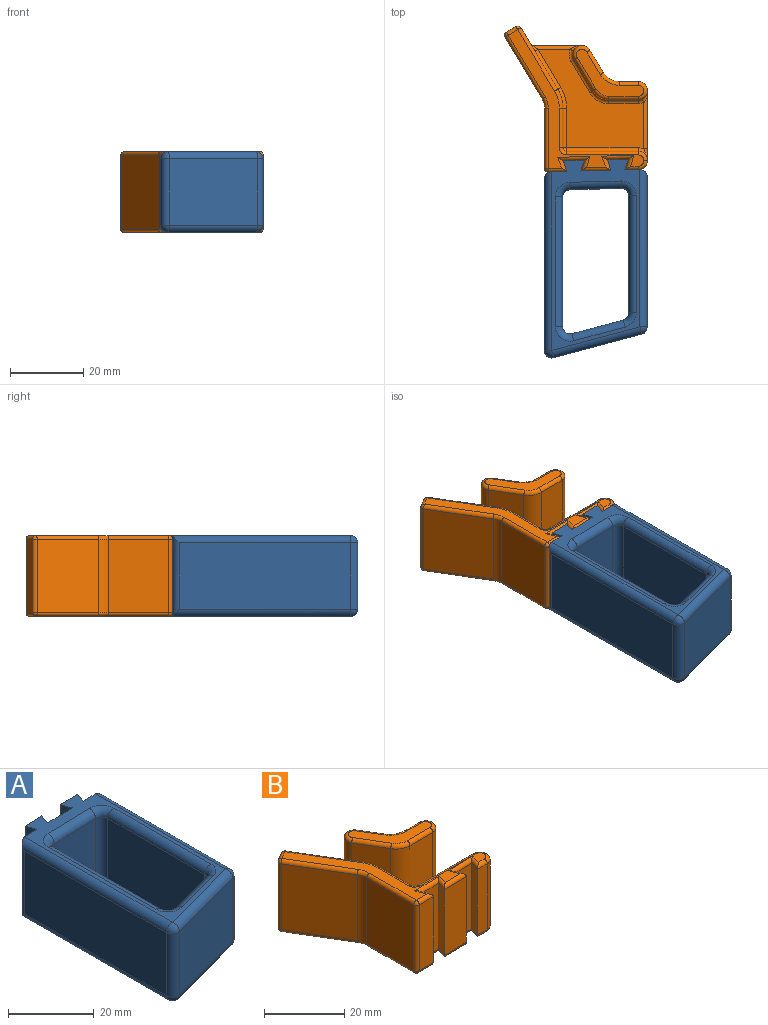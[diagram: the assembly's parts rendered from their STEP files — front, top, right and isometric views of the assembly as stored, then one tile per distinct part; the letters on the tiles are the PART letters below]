
ASSEMBLY  parts=2 mates=1
PART A: 52 faces, bbox 28x54.2x22 mm
  f0: plane 52.16x24.01mm, normal (0,0,-1), area 222.9mm2, adj f5,f6,f7,f8,f9,f13,f14,f15
  f1: plane 52.16x24.01mm, normal (0,0,1), area 222.9mm2, adj f5,f6,f7,f8,f9,f13,f14,f15
  f2: plane 35.33x18mm, normal (1,0,0), area 635.9mm2, adj f18,f21,f25,f26
  f3: plane 18x14.01mm, normal (0.03,-1,0), area 252.2mm2, adj f24,f25,f33,f34
  f4: plane 31.94x18mm, normal (-1,0,0), area 574.9mm2, adj f23,f32,f33,f37
  f5: plane 22x8.21mm, normal (-0.03,1,0), area 180.7mm2, adj f0,f1,f6,f16
  f6: plane 22x2.93mm, normal (0.95,-0.31,0), area 67.8mm2, adj f0,f1,f5,f7
  f7: plane 22x5.72mm, normal (-0.03,1,0), area 125.9mm2, adj f0,f1,f6,f8
  f8: plane 22x2.88mm, normal (-0.95,-0.32,0), area 66.7mm2, adj f0,f1,f7,f9
  f9: plane 22x4.2mm, normal (-0.03,1,0), area 92.4mm2, adj f0,f1,f8,f49,f50,f51
  f10: plane 46.71x18mm, normal (-1,0,0), area 840.9mm2, adj f45,f49,f50,f51
  f11: plane 24.01x18mm, normal (0.26,-0.97,0), area 447.3mm2, adj f40,f44,f45,f46
  f12: plane 40.91x18mm, normal (1,0,0), area 736.4mm2, adj f38,f39,f40,f41
  f13: plane 22x4.02mm, normal (-0.03,1,0), area 88.4mm2, adj f0,f1,f14,f38
  f14: plane 22x2.93mm, normal (0.95,-0.31,0), area 67.8mm2, adj f0,f1,f13,f15
  f15: plane 22x5.72mm, normal (-0.03,1,0), area 126mm2, adj f0,f1,f14,f16
  f16: plane 22x2.88mm, normal (-0.95,-0.32,0), area 66.8mm2, adj f0,f1,f5,f15
  f17: plane 18x14.01mm, normal (-0.26,0.97,0), area 261mm2, adj f21,f22,f31,f32
  f18: cylinder r=2mm len=35.33mm, axis (0,1,0), area 111mm2, adj f0,f2,f19,f20
  f19: torus R=4mm, axis (0,0,1), area 15.7mm2, adj f0,f18,f21,f22
  f20: torus R=4mm, axis (0,0,1), area 13.2mm2, adj f0,f18,f24,f25
  f21: cylinder r=2mm len=18mm, axis (0,0,1), area 66mm2, adj f2,f17,f19,f27
  f22: cylinder r=2mm len=14.52mm, axis (-0.97,-0.26,0), area 45.6mm2, adj f0,f17,f19,f28
  f23: cylinder r=2mm len=31.94mm, axis (0,-1,0), area 100.3mm2, adj f0,f4,f28,f29
  f24: cylinder r=2mm len=14.06mm, axis (1,0.03,0), area 44mm2, adj f0,f3,f20,f29
  f25: cylinder r=2mm len=18mm, axis (0,0,1), area 55.6mm2, adj f2,f3,f20,f30
  f26: cylinder r=2mm len=35.33mm, axis (0,-1,0), area 111mm2, adj f1,f2,f27,f30
  f27: torus R=4mm, axis (0,0,1), area 15.7mm2, adj f1,f21,f26,f31
  f28: torus R=4mm, axis (0,0,1), area 11.2mm2, adj f0,f22,f23,f32
  f29: torus R=4mm, axis (0,0,1), area 13.7mm2, adj f0,f23,f24,f33
  f30: torus R=4mm, axis (0,0,1), area 13.2mm2, adj f1,f25,f26,f34
  f31: cylinder r=2mm len=14.52mm, axis (0.97,0.26,0), area 45.6mm2, adj f1,f17,f27,f35
  f32: cylinder r=2mm len=18mm, axis (0,0,1), area 47.1mm2, adj f4,f17,f28,f35
  f33: cylinder r=2mm len=18mm, axis (0,0,1), area 57.5mm2, adj f3,f4,f29,f36
  f34: cylinder r=2mm len=14.06mm, axis (-1,-0.03,0), area 44mm2, adj f1,f3,f30,f36
  f35: torus R=4mm, axis (0,0,1), area 11.2mm2, adj f1,f31,f32,f37
  f36: torus R=4mm, axis (0,0,1), area 13.7mm2, adj f1,f33,f34,f37
  f37: cylinder r=2mm len=31.94mm, axis (0,1,0), area 100.3mm2, adj f1,f4,f35,f36
  f38: cylinder r=2mm len=22mm, axis (0,0,1), area 65.7mm2, adj f0,f1,f12,f13,f39,f41
  f39: cylinder r=2mm len=42.91mm, axis (0,-1,0), area 132.5mm2, adj f1,f12,f38,f42
  f40: cylinder r=2mm len=18mm, axis (0,0,-1), area 47.1mm2, adj f11,f12,f42,f43
  f41: cylinder r=2mm len=42.91mm, axis (0,1,0), area 132.5mm2, adj f0,f12,f38,f43
  f42: sphere r=2mm, area 5.2mm2, adj f39,f40,f44
  f43: sphere r=2mm, area 5.2mm2, adj f40,f41,f46
  f44: cylinder r=2mm len=24.52mm, axis (-0.97,-0.26,0), area 78.1mm2, adj f1,f11,f42,f47
  f45: cylinder r=2mm len=18mm, axis (0,0,-1), area 66mm2, adj f10,f11,f47,f48
  f46: cylinder r=2mm len=24.52mm, axis (0.97,0.26,0), area 78.1mm2, adj f0,f11,f43,f48
  f47: sphere r=2mm, area 7.3mm2, adj f44,f45,f49
  f48: sphere r=2mm, area 7.3mm2, adj f45,f46,f50
  f49: cylinder r=2mm len=48.72mm, axis (0,1,0), area 150.8mm2, adj f1,f9,f10,f47,f51
  f50: cylinder r=2mm len=48.72mm, axis (0,-1,0), area 150.8mm2, adj f0,f9,f10,f48,f51
  f51: cylinder r=2mm len=22mm, axis (0,0,1), area 63.4mm2, adj f9,f10,f49,f50
PART B: 113 faces, bbox 41x40.1x22 mm
  f0: plane 20x5.02mm, normal (0.03,-1,0), area 100.4mm2, adj f31,f44,f53,f54
  f1: plane 20x8mm, normal (0.03,-1,0), area 160mm2, adj f27,f32,f33,f38
  f2: plane 37.85x36.92mm, normal (0,0,1), area 149.9mm2, adj f33,f34,f35,f36,f37,f39,f40,f43
  f3: plane 37.85x36.92mm, normal (0,0,-1), area 741.3mm2, adj f38,f41,f42,f45,f46,f49,f50,f54
  f4: plane 20x16.77mm, normal (0.86,0.51,0), area 319.8mm2, adj f19,f79,f91,f99,f100,f102,f104
  f5: plane 15x10.74mm, normal (1,0,0), area 161.2mm2, adj f19,f65,f78,f90
  f6: plane 20x2.57mm, normal (-0.51,0.86,0), area 60mm2, adj f80,f81,f91,f92
  f7: plane 20x16.77mm, normal (-0.86,-0.51,0), area 391.1mm2, adj f20,f66,f81,f82
  f8: plane 20x16.45mm, normal (-1,0,0), area 329mm2, adj f20,f52,f53,f67
  f9: plane 20x3.53mm, normal (0.03,-1,0), area 70.6mm2, adj f23,f28,f43,f55
  f10: plane 20x19.06mm, normal (1,0,0), area 60.4mm2, adj f23,f24,f25,f51,f57,f63,f68
  f11: plane 19.5x15mm, normal (0,1,0), area 292.5mm2, adj f24,f64,f77,f78
  f12: plane 20x6.16mm, normal (0.86,0.51,0), area 143.7mm2, adj f21,f26,f93,f107
  f13: plane 13.18x3mm, normal (0,1,0), area 39.5mm2, adj f26,f98,f101,f104
  f14: plane 15x8.59mm, normal (-0.86,-0.51,0), area 150.2mm2, adj f22,f26,f84,f106
  f15: plane 15x8.03mm, normal (0,-1,0), area 120.5mm2, adj f22,f25,f69,f110
  f16: plane 20x5.2mm, normal (0,1,0), area 104mm2, adj f21,f25,f83,f111
  f17: plane 18.33x12.8mm, normal (0,0,1), area 70.7mm2, adj f105,f106,f107,f108,f109,f110,f111,f112
  f18: plane 28.81x27.14mm, normal (0,0,1), area 361.6mm2, adj f57,f62,f69,f70,f76,f77,f84,f89
  f19: cylinder r=10mm len=15mm, axis (0,0,-1), area 81.1mm2, adj f4,f5,f72,f95
  f20: cylinder r=5mm len=20mm, axis (0,0,1), area 54mm2, adj f7,f8,f59,f74
  f21: cylinder r=5mm len=20mm, axis (0,0,-1), area 103mm2, adj f12,f16,f88,f109
  f22: cylinder r=5mm len=15mm, axis (0,0,1), area 77.3mm2, adj f14,f15,f76,f108
  f23: cylinder r=2.5mm len=20mm, axis (0,0,-1), area 77.2mm2, adj f9,f10,f47,f61
  f24: cylinder r=2.5mm len=15mm, axis (0,0,-1), area 58.9mm2, adj f10,f11,f58,f70
  f25: cylinder r=2.5mm len=20mm, axis (0,0,1), area 139.6mm2, adj f10,f15,f16,f56,f62,f75,f112
  f26: cylinder r=2.5mm len=20mm, axis (0,0,-1), area 132.8mm2, adj f12,f13,f14,f89,f94,f97,f105
  f27: plane 20x2.97mm, normal (0.94,0.34,0), area 63.2mm2, adj f1,f29,f34,f42
  f28: plane 20x3.03mm, normal (-0.96,0.29,0), area 63.2mm2, adj f9,f29,f39,f50
  f29: plane 20x6mm, normal (0.03,-1,0), area 120mm2, adj f27,f28,f36,f46
  f30: plane 20x6mm, normal (0.03,-1,0), area 120mm2, adj f31,f32,f37,f45
  f31: plane 20x2.97mm, normal (0.94,0.34,0), area 63.2mm2, adj f0,f30,f40,f49
  f32: plane 20x3.03mm, normal (-0.96,0.29,0), area 63.2mm2, adj f1,f30,f35,f41
  f33: cylinder r=1mm len=8.02mm, axis (-1,-0.03,0), area 11mm2, adj f1,f2,f34,f35
  f34: cylinder r=1mm len=4.62mm, axis (-0.34,0.94,0), area 5mm2, adj f2,f27,f33,f36
  f35: cylinder r=1mm len=4.64mm, axis (-0.29,-0.96,0), area 5mm2, adj f2,f32,f33,f37
  f36: cylinder r=1mm len=8.8mm, axis (1,0.03,0), area 11mm2, adj f2,f29,f34,f39
  f37: cylinder r=1mm len=8.8mm, axis (1,0.03,0), area 11mm2, adj f2,f30,f35,f40
  f38: cylinder r=1mm len=8.02mm, axis (1,0.03,0), area 11mm2, adj f1,f3,f41,f42
  f39: cylinder r=1mm len=4.64mm, axis (-0.29,-0.96,0), area 5mm2, adj f2,f28,f36,f43
  f40: cylinder r=1mm len=4.62mm, axis (-0.34,0.94,0), area 5mm2, adj f2,f31,f37,f44
  f41: cylinder r=1mm len=4.64mm, axis (0.29,0.96,0), area 5mm2, adj f3,f32,f38,f45
  f42: cylinder r=1mm len=4.62mm, axis (0.34,-0.94,0), area 5mm2, adj f3,f27,f38,f46
  f43: cylinder r=1mm len=3.56mm, axis (-1,-0.03,0), area 4.8mm2, adj f2,f9,f39,f47
  f44: cylinder r=1mm len=5.04mm, axis (-1,-0.03,0), area 7.1mm2, adj f0,f2,f40,f48
  f45: cylinder r=1mm len=8.8mm, axis (-1,-0.03,0), area 11mm2, adj f3,f30,f41,f49
  f46: cylinder r=1mm len=8.8mm, axis (-1,-0.03,0), area 11mm2, adj f3,f29,f42,f50
  f47: torus R=1.5mm, axis (0,0,1), area 5.2mm2, adj f2,f23,f43,f51
  f48: sphere r=1mm, area 1.6mm2, adj f44,f52,f53
  f49: cylinder r=1mm len=4.62mm, axis (0.34,-0.94,0), area 5mm2, adj f3,f31,f45,f54
  f50: cylinder r=1mm len=4.64mm, axis (0.29,0.96,0), area 5mm2, adj f3,f28,f46,f55
  f51: cylinder r=1mm len=1mm, axis (0,-1,0), area 0.1mm2, adj f2,f10,f47,f58
  f52: cylinder r=1mm len=16.45mm, axis (0,1,0), area 25.8mm2, adj f2,f8,f48,f59
  f53: cylinder r=1mm len=20mm, axis (0,0,1), area 31.9mm2, adj f0,f8,f48,f60
  f54: cylinder r=1mm len=5.04mm, axis (1,0.03,0), area 7.1mm2, adj f0,f3,f49,f60
  f55: cylinder r=1mm len=3.56mm, axis (1,0.03,0), area 4.8mm2, adj f3,f9,f50,f61
  f56: bspline ~3.16x2mm, area 2.6mm2, adj f25,f57,f62
  f57: cylinder r=1mm len=15.84mm, axis (0,-1,0), area 22mm2, adj f10,f18,f56,f63
  f58: torus R=1.5mm, axis (0,0,1), area 5.3mm2, adj f2,f24,f51,f64
  f59: torus R=6mm, axis (0,0,1), area 4.6mm2, adj f2,f20,f52,f66
  f60: sphere r=1mm, area 1.6mm2, adj f53,f54,f67
  f61: torus R=1.5mm, axis (0,0,1), area 5.2mm2, adj f3,f23,f55,f68
  f62: torus R=3.5mm, axis (0,0,1), area 2mm2, adj f18,f25,f56,f69
  f63: bspline ~3.16x2mm, area 3mm2, adj f10,f57,f70
  f64: cylinder r=1mm len=19.5mm, axis (1,0,0), area 30.6mm2, adj f2,f11,f58,f71
  f65: cylinder r=1mm len=10.74mm, axis (0,-1,0), area 16.9mm2, adj f2,f5,f71,f72
  f66: cylinder r=1mm len=17.28mm, axis (-0.51,0.86,0), area 30.7mm2, adj f2,f7,f59,f73
  f67: cylinder r=1mm len=16.45mm, axis (0,-1,0), area 25.8mm2, adj f3,f8,f60,f74
  f68: cylinder r=1mm len=19.06mm, axis (0,1,0), area 29.9mm2, adj f3,f10,f61,f75
  f69: cylinder r=1mm len=8.03mm, axis (1,0,0), area 12.6mm2, adj f15,f18,f62,f76
  f70: torus R=3.5mm, axis (0,0,1), area 3.8mm2, adj f18,f24,f63,f77
  f71: torus R=2mm, axis (0,0,1), area 3.4mm2, adj f2,f64,f65,f78
  f72: torus R=9mm, axis (0,0,1), area 8.2mm2, adj f2,f19,f65,f79
  f73: sphere r=1mm, area 1.6mm2, adj f66,f80,f81
  f74: torus R=6mm, axis (0,0,1), area 4.6mm2, adj f3,f20,f67,f82
  f75: torus R=1.5mm, axis (0,0,1), area 5.3mm2, adj f3,f25,f68,f83
  f76: torus R=6mm, axis (0,0,1), area 8.7mm2, adj f18,f22,f69,f84
  f77: cylinder r=1mm len=19.5mm, axis (-1,0,0), area 30.6mm2, adj f11,f18,f70,f85
  f78: cylinder r=1mm len=15mm, axis (0,0,1), area 23.6mm2, adj f5,f11,f71,f85
  f79: cylinder r=1mm len=17.28mm, axis (0.51,-0.86,0), area 30.7mm2, adj f2,f4,f72,f86
  f80: cylinder r=1mm len=3.09mm, axis (0.86,0.51,0), area 4.7mm2, adj f2,f6,f73,f86
  f81: cylinder r=1mm len=20mm, axis (0,0,-1), area 31.4mm2, adj f6,f7,f73,f87
  f82: cylinder r=1mm len=17.28mm, axis (0.51,-0.86,0), area 30.7mm2, adj f3,f7,f74,f87
  f83: cylinder r=1mm len=5.2mm, axis (-1,0,0), area 8.2mm2, adj f3,f16,f75,f88
  f84: cylinder r=1mm len=9.1mm, axis (-0.51,0.86,0), area 15.7mm2, adj f14,f18,f76,f89
  f85: sphere r=1mm, area 1.6mm2, adj f77,f78,f90
  f86: sphere r=1mm, area 1.6mm2, adj f79,f80,f91
  f87: sphere r=1mm, area 1.6mm2, adj f81,f82,f92
  f88: torus R=6mm, axis (0,0,1), area 8.7mm2, adj f3,f21,f83,f93
  f89: torus R=3.5mm, axis (0,0,1), area 4.4mm2, adj f18,f26,f84,f94
  f90: cylinder r=1mm len=10.74mm, axis (0,1,0), area 16.9mm2, adj f5,f18,f85,f95
  f91: cylinder r=1mm len=20mm, axis (0,0,1), area 31.4mm2, adj f4,f6,f86,f96
  f92: cylinder r=1mm len=3.09mm, axis (-0.86,-0.51,0), area 4.7mm2, adj f3,f6,f87,f96
  f93: cylinder r=1mm len=6.68mm, axis (-0.51,0.86,0), area 11.3mm2, adj f3,f12,f88,f97
  f94: bspline ~3.16x2mm, area 2.6mm2, adj f26,f89,f98
  f95: torus R=11mm, axis (0,0,1), area 8.8mm2, adj f18,f19,f90,f99
  f96: sphere r=1mm, area 1.6mm2, adj f91,f92,f100
  f97: torus R=1.5mm, axis (0,0,1), area 3.5mm2, adj f3,f26,f93,f101
  f98: cylinder r=1mm len=13.18mm, axis (1,0,0), area 17.2mm2, adj f13,f18,f94,f102
  f99: cylinder r=1mm len=10.91mm, axis (-0.51,0.86,0), area 19mm2, adj f4,f18,f95,f102
  f100: cylinder r=1mm len=4.88mm, axis (-0.51,0.86,0), area 8mm2, adj f3,f4,f96,f103
  f101: cylinder r=1mm len=13.18mm, axis (-1,0,0), area 20.7mm2, adj f3,f13,f97,f103
  f102: bspline ~2.35x2.35mm, area 3.2mm2, adj f4,f98,f99,f104
  f103: torus R=2mm, axis (0,0,1), area 2.2mm2, adj f3,f100,f101,f104
  f104: cylinder r=1mm len=3mm, axis (0,0,-1), area 3.1mm2, adj f4,f13,f102,f103
  f105: torus R=1.5mm, axis (0,0,1), area 10.5mm2, adj f17,f26,f106,f107
  f106: cylinder r=1mm len=9.1mm, axis (-0.51,0.86,0), area 15.7mm2, adj f14,f17,f105,f108
  f107: cylinder r=1mm len=6.68mm, axis (0.51,-0.86,0), area 11.3mm2, adj f12,f17,f105,f109
  f108: torus R=4mm, axis (0,0,1), area 7.5mm2, adj f17,f22,f106,f110
  f109: torus R=6mm, axis (0,0,1), area 8.7mm2, adj f17,f21,f107,f111
  f110: cylinder r=1mm len=8.03mm, axis (-1,0,0), area 12.6mm2, adj f15,f17,f108,f112
  f111: cylinder r=1mm len=5.2mm, axis (1,0,0), area 8.2mm2, adj f16,f17,f109,f112
  f112: torus R=1.5mm, axis (0,0,1), area 10.5mm2, adj f17,f25,f110,f111
PLACE A at identity
PLACE B t=(-32.3,-39.84,0)mm
MATE fastened B.f30 <-> A.f7  axis (0.03,-1,0) through (-32.33,-56.88,11)mm
